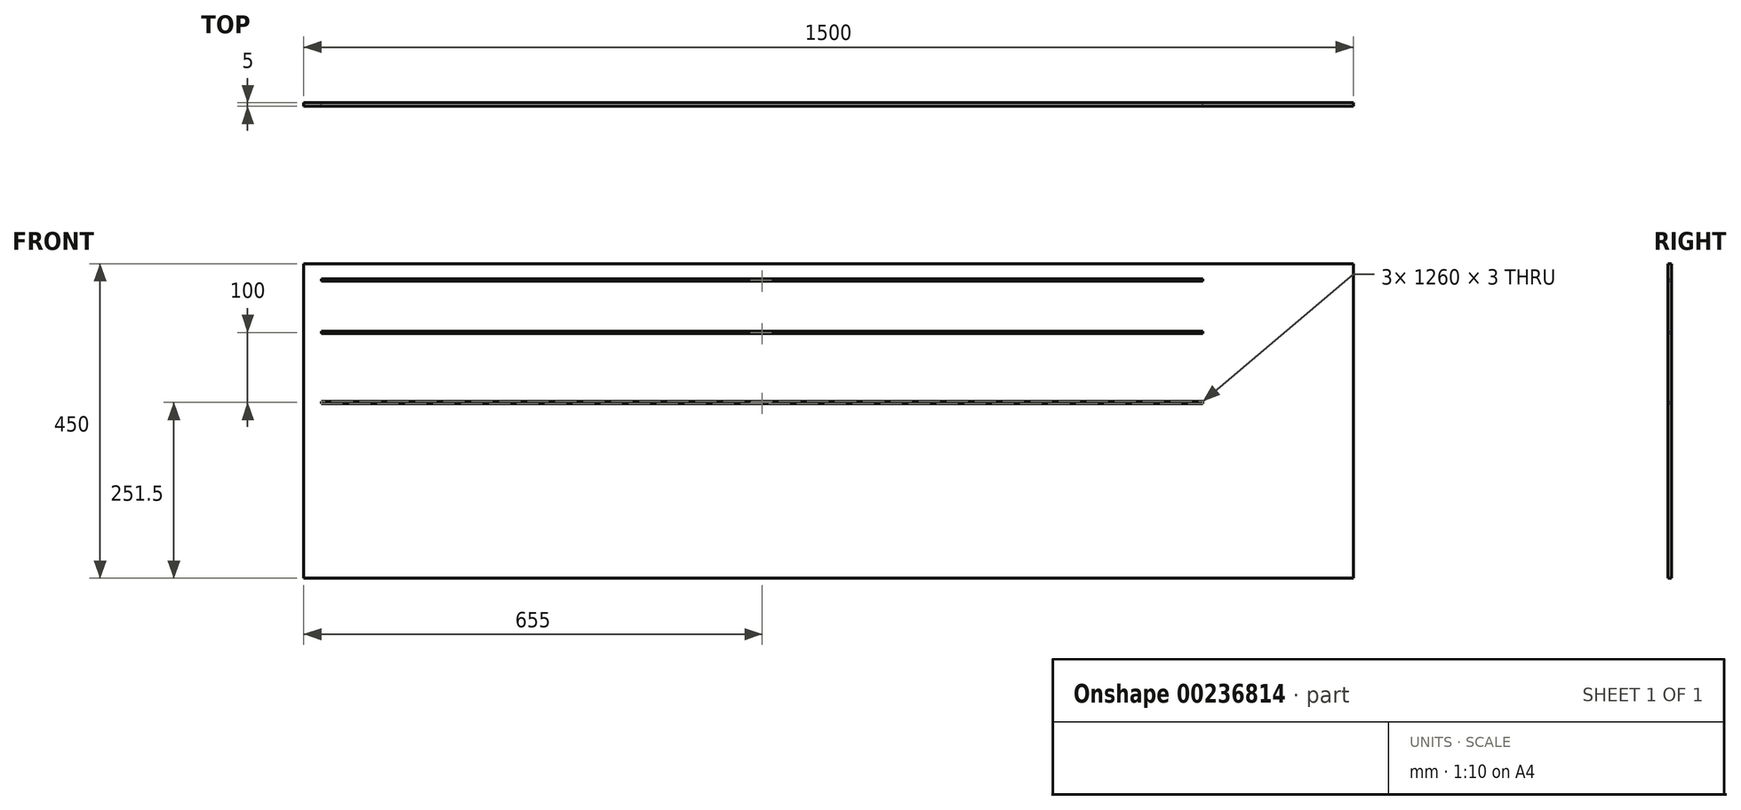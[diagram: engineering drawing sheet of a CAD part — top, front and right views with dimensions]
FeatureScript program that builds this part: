
annotation { "Feature Type Name" : "Feature", "Feature Type Description" : "" }
export const myFeature = defineFeature(function(context is Context, id is Id, definition is map)
    precondition{}
    {
        {
            var Q0;
            Q0=qCreatedBy(makeId("Front.planeOp"),FACE);
            var sketch = newSketch(context, id + "F0", { "sketchPlane" : qUnion([Q0])});
            skLineSegment(sketch, "E0.bottom", {"start": v(0, 0) * mm, "end": v(1500, 0) * mm});
            skLineSegment(sketch, "E0.top", {"start": v(0, 450) * mm, "end": v(1500, 450) * mm});
            skLineSegment(sketch, "E0.left", {"start": v(0, 0) * mm, "end": v(0, 450) * mm});
            skLineSegment(sketch, "E0.right", {"start": v(1500, 0) * mm, "end": v(1500, 450) * mm});
            skLineSegment(sketch, "E1.bottom", {"start": v(25, 253) * mm, "end": v(1285, 253) * mm});
            skLineSegment(sketch, "E1.top", {"start": v(25, 250) * mm, "end": v(1285, 250) * mm});
            skLineSegment(sketch, "E1.left", {"start": v(25, 253) * mm, "end": v(25, 250) * mm});
            skLineSegment(sketch, "E1.right", {"start": v(1285, 253) * mm, "end": v(1285, 250) * mm});
            skLineSegment(sketch, "E2.bottom", {"start": v(25, 353) * mm, "end": v(1285, 353) * mm});
            skLineSegment(sketch, "E2.top", {"start": v(25, 350) * mm, "end": v(1285, 350) * mm});
            skLineSegment(sketch, "E2.left", {"start": v(25, 353) * mm, "end": v(25, 350) * mm});
            skLineSegment(sketch, "E2.right", {"start": v(1285, 353) * mm, "end": v(1285, 350) * mm});
            skLineSegment(sketch, "E3.bottom", {"start": v(25, 428) * mm, "end": v(1285, 428) * mm});
            skLineSegment(sketch, "E3.top", {"start": v(25, 425) * mm, "end": v(1285, 425) * mm});
            skLineSegment(sketch, "E3.left", {"start": v(25, 428) * mm, "end": v(25, 425) * mm});
            skLineSegment(sketch, "E3.right", {"start": v(1285, 428) * mm, "end": v(1285, 425) * mm});
            skSolve(sketch);
        }
        {
            var Q0;
            Q0=makeQuery(id+"F0.imprint","IMPRINT",FACE,{"disambiguationData":[TD([[makeQuery(id+"F0.imprint","IMPRINT",EDGE,{"derivedFrom":sQuery(id+"F0.wireOp",EDGE,"E0.bottom")}),1.0]])]});
            extrude(context, id + "F1", {"entities" : qUnion([Q0]), "depth" : 5 * mm});
        }
    });
